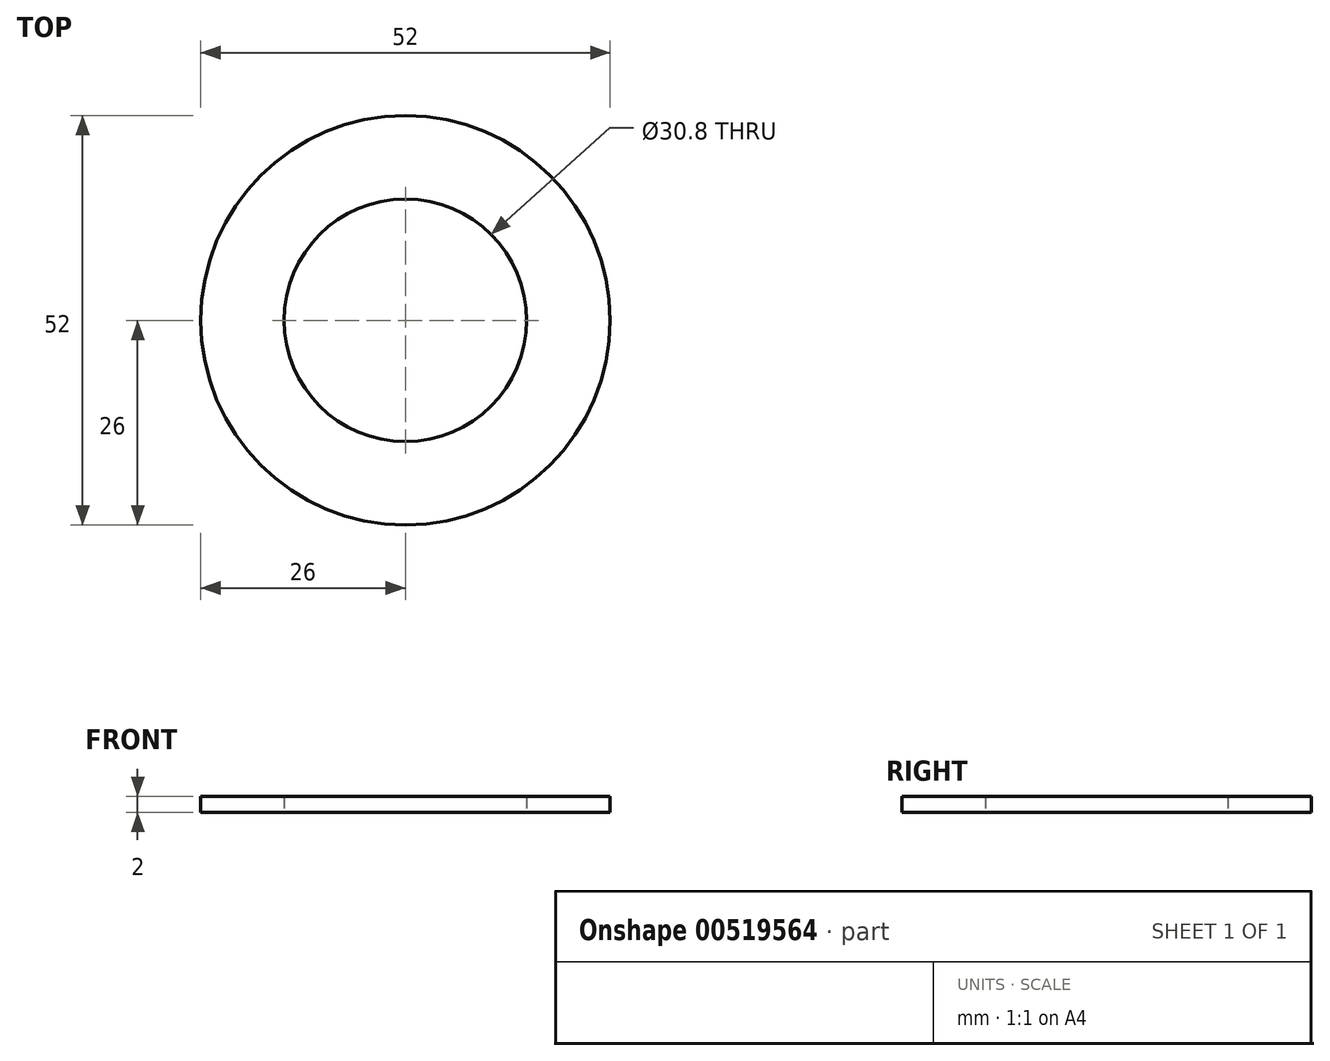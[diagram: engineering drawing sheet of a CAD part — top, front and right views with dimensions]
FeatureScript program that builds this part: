
annotation { "Feature Type Name" : "Feature", "Feature Type Description" : "" }
export const myFeature = defineFeature(function(context is Context, id is Id, definition is map)
    precondition{}
    {
        {
            var Q0;
            Q0=qCreatedBy(makeId("Top.planeOp"),FACE);
            var sketch = newSketch(context, id + "F0", { "sketchPlane" : qUnion([Q0])});
            skCircle(sketch, "E0", {"center": v(0, 0) * mm, "radius": 15.4 * mm});
            skCircle(sketch, "E1", {"center": v(0, 0) * mm, "radius": 26 * mm});
            skSolve(sketch);
        }
        {
            var Q0;
            Q0=makeQuery(id+"F0.imprint","IMPRINT",FACE,{"disambiguationData":[TD([[makeQuery(id+"F0.imprint","IMPRINT",EDGE,{"derivedFrom":sQuery(id+"F0.wireOp",EDGE,"E0")}),-1.0]])]});
            extrude(context, id + "F1", {"entities" : qUnion([Q0]), "depth" : 2 * mm, "offsetDistance" : 25 * mm});
        }
    });
